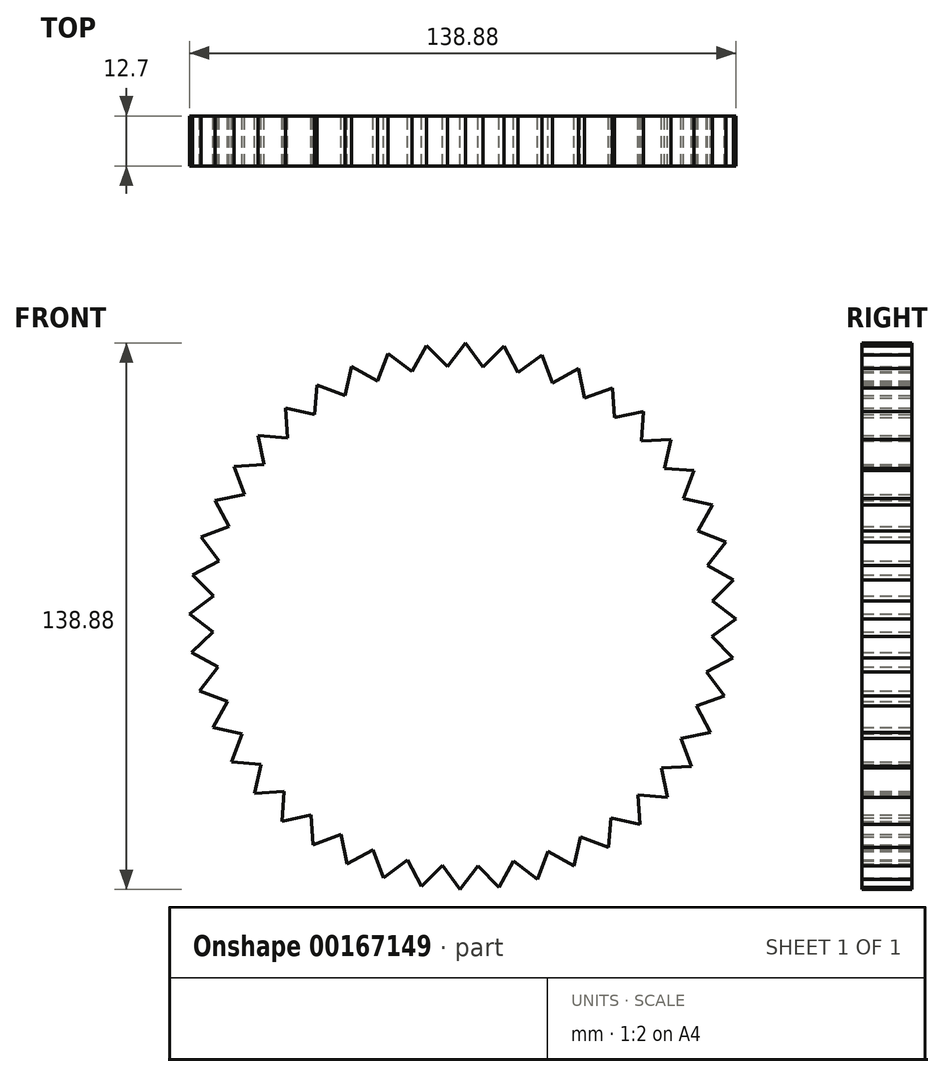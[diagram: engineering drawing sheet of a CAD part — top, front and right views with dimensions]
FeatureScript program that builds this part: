
annotation { "Feature Type Name" : "Feature", "Feature Type Description" : "" }
export const myFeature = defineFeature(function(context is Context, id is Id, definition is map)
    precondition{}
    {
        {
            var Q0;
            Q0=qCreatedBy(makeId("Front.planeOp"),FACE);
            var sketch = newSketch(context, id + "F0", { "sketchPlane" : qUnion([Q0])});
            skCircle(sketch, "E0", {"center": v(0, 0) * mm, "radius": 63.5 * mm});
            skCircle(sketch, "E1", {"center": v(0, 0) * mm, "radius": 25.4 * mm});
            skLineSegment(sketch, "E2", {"start": v(-55.46, 30.93) * mm, "end": v(-58.06, 38.1) * mm});
            skLineSegment(sketch, "E3", {"start": v(-58.06, 38.1) * mm, "end": v(-50.46, 38.55) * mm});
            skLineSegment(sketch, "E4.1.0", {"start": v(-59.3, 22.72) * mm, "end": v(-62.9, 29.44) * mm});
            skLineSegment(sketch, "E4.1.1", {"start": v(-62.9, 29.44) * mm, "end": v(-55.43, 30.98) * mm});
            skLineSegment(sketch, "E4.2.0", {"start": v(-61.93, 14.05) * mm, "end": v(-66.44, 20.2) * mm});
            skLineSegment(sketch, "E4.2.1", {"start": v(-66.44, 20.2) * mm, "end": v(-59.28, 22.77) * mm});
            skLineSegment(sketch, "E4.3.0", {"start": v(-63.3, 5.1) * mm, "end": v(-68.64, 10.53) * mm});
            skLineSegment(sketch, "E4.3.1", {"start": v(-68.64, 10.53) * mm, "end": v(-61.91, 14.1) * mm});
            skLineSegment(sketch, "E4.4.0", {"start": v(-63.38, -3.96) * mm, "end": v(-69.44, 0.65) * mm});
            skLineSegment(sketch, "E4.4.1", {"start": v(-69.44, 0.65) * mm, "end": v(-63.3, 5.15) * mm});
            skLineSegment(sketch, "E4.5.0", {"start": v(-62.17, -12.94) * mm, "end": v(-68.83, -9.24) * mm});
            skLineSegment(sketch, "E4.5.1", {"start": v(-68.83, -9.24) * mm, "end": v(-63.38, -3.9) * mm});
            skLineSegment(sketch, "E4.6.0", {"start": v(-59.7, -21.66) * mm, "end": v(-66.81, -18.94) * mm});
            skLineSegment(sketch, "E4.6.1", {"start": v(-66.81, -18.94) * mm, "end": v(-62.18, -12.89) * mm});
            skLineSegment(sketch, "E4.7.0", {"start": v(-56, -29.93) * mm, "end": v(-63.44, -28.25) * mm});
            skLineSegment(sketch, "E4.7.1", {"start": v(-63.44, -28.25) * mm, "end": v(-59.71, -21.6) * mm});
            skLineSegment(sketch, "E4.8.0", {"start": v(-51.17, -37.6) * mm, "end": v(-58.77, -37) * mm});
            skLineSegment(sketch, "E4.8.1", {"start": v(-58.77, -37) * mm, "end": v(-56.03, -29.88) * mm});
            skLineSegment(sketch, "E4.9.0", {"start": v(-45.3, -44.5) * mm, "end": v(-52.9, -44.98) * mm});
            skLineSegment(sketch, "E4.9.1", {"start": v(-52.9, -44.98) * mm, "end": v(-51.2, -37.55) * mm});
            skLineSegment(sketch, "E4.10.0", {"start": v(-38.5, -50.5) * mm, "end": v(-45.97, -52.05) * mm});
            skLineSegment(sketch, "E4.10.1", {"start": v(-45.97, -52.05) * mm, "end": v(-45.34, -44.46) * mm});
            skLineSegment(sketch, "E4.11.0", {"start": v(-30.93, -55.46) * mm, "end": v(-38.1, -58.06) * mm});
            skLineSegment(sketch, "E4.11.1", {"start": v(-38.1, -58.06) * mm, "end": v(-38.55, -50.46) * mm});
            skLineSegment(sketch, "E4.12.0", {"start": v(-22.72, -59.3) * mm, "end": v(-29.44, -62.9) * mm});
            skLineSegment(sketch, "E4.12.1", {"start": v(-29.44, -62.9) * mm, "end": v(-30.98, -55.43) * mm});
            skLineSegment(sketch, "E4.13.0", {"start": v(-14.05, -61.93) * mm, "end": v(-20.2, -66.44) * mm});
            skLineSegment(sketch, "E4.13.1", {"start": v(-20.2, -66.44) * mm, "end": v(-22.77, -59.28) * mm});
            skLineSegment(sketch, "E4.14.0", {"start": v(-5.1, -63.3) * mm, "end": v(-10.53, -68.64) * mm});
            skLineSegment(sketch, "E4.14.1", {"start": v(-10.53, -68.64) * mm, "end": v(-14.1, -61.91) * mm});
            skLineSegment(sketch, "E4.15.0", {"start": v(3.96, -63.38) * mm, "end": v(-0.65, -69.44) * mm});
            skLineSegment(sketch, "E4.15.1", {"start": v(-0.65, -69.44) * mm, "end": v(-5.15, -63.3) * mm});
            skLineSegment(sketch, "E4.16.0", {"start": v(12.94, -62.17) * mm, "end": v(9.24, -68.83) * mm});
            skLineSegment(sketch, "E4.16.1", {"start": v(9.24, -68.83) * mm, "end": v(3.9, -63.38) * mm});
            skLineSegment(sketch, "E4.17.0", {"start": v(21.66, -59.7) * mm, "end": v(18.94, -66.81) * mm});
            skLineSegment(sketch, "E4.17.1", {"start": v(18.94, -66.81) * mm, "end": v(12.89, -62.18) * mm});
            skLineSegment(sketch, "E4.18.0", {"start": v(29.93, -56) * mm, "end": v(28.25, -63.44) * mm});
            skLineSegment(sketch, "E4.18.1", {"start": v(28.25, -63.44) * mm, "end": v(21.6, -59.71) * mm});
            skLineSegment(sketch, "E4.19.0", {"start": v(37.6, -51.17) * mm, "end": v(37, -58.77) * mm});
            skLineSegment(sketch, "E4.19.1", {"start": v(37, -58.77) * mm, "end": v(29.88, -56.03) * mm});
            skLineSegment(sketch, "E4.20.0", {"start": v(44.5, -45.3) * mm, "end": v(44.98, -52.9) * mm});
            skLineSegment(sketch, "E4.20.1", {"start": v(44.98, -52.9) * mm, "end": v(37.55, -51.2) * mm});
            skLineSegment(sketch, "E4.21.0", {"start": v(50.5, -38.5) * mm, "end": v(52.05, -45.97) * mm});
            skLineSegment(sketch, "E4.21.1", {"start": v(52.05, -45.97) * mm, "end": v(44.46, -45.34) * mm});
            skLineSegment(sketch, "E4.22.0", {"start": v(55.46, -30.93) * mm, "end": v(58.06, -38.1) * mm});
            skLineSegment(sketch, "E4.22.1", {"start": v(58.06, -38.1) * mm, "end": v(50.46, -38.55) * mm});
            skLineSegment(sketch, "E4.23.0", {"start": v(59.3, -22.72) * mm, "end": v(62.9, -29.44) * mm});
            skLineSegment(sketch, "E4.23.1", {"start": v(62.9, -29.44) * mm, "end": v(55.43, -30.98) * mm});
            skLineSegment(sketch, "E4.24.0", {"start": v(61.93, -14.05) * mm, "end": v(66.44, -20.2) * mm});
            skLineSegment(sketch, "E4.24.1", {"start": v(66.44, -20.2) * mm, "end": v(59.28, -22.77) * mm});
            skLineSegment(sketch, "E4.25.0", {"start": v(63.3, -5.1) * mm, "end": v(68.64, -10.53) * mm});
            skLineSegment(sketch, "E4.25.1", {"start": v(68.64, -10.53) * mm, "end": v(61.91, -14.1) * mm});
            skLineSegment(sketch, "E4.26.0", {"start": v(63.38, 3.96) * mm, "end": v(69.44, -0.65) * mm});
            skLineSegment(sketch, "E4.26.1", {"start": v(69.44, -0.65) * mm, "end": v(63.3, -5.15) * mm});
            skLineSegment(sketch, "E4.27.0", {"start": v(62.17, 12.94) * mm, "end": v(68.83, 9.24) * mm});
            skLineSegment(sketch, "E4.27.1", {"start": v(68.83, 9.24) * mm, "end": v(63.38, 3.9) * mm});
            skLineSegment(sketch, "E4.28.0", {"start": v(59.7, 21.66) * mm, "end": v(66.81, 18.94) * mm});
            skLineSegment(sketch, "E4.28.1", {"start": v(66.81, 18.94) * mm, "end": v(62.18, 12.89) * mm});
            skLineSegment(sketch, "E4.29.0", {"start": v(56, 29.93) * mm, "end": v(63.44, 28.25) * mm});
            skLineSegment(sketch, "E4.29.1", {"start": v(63.44, 28.25) * mm, "end": v(59.71, 21.6) * mm});
            skLineSegment(sketch, "E4.30.0", {"start": v(51.17, 37.6) * mm, "end": v(58.77, 37) * mm});
            skLineSegment(sketch, "E4.30.1", {"start": v(58.77, 37) * mm, "end": v(56.03, 29.88) * mm});
            skLineSegment(sketch, "E4.31.0", {"start": v(45.3, 44.5) * mm, "end": v(52.9, 44.98) * mm});
            skLineSegment(sketch, "E4.31.1", {"start": v(52.9, 44.98) * mm, "end": v(51.2, 37.55) * mm});
            skLineSegment(sketch, "E4.32.0", {"start": v(38.5, 50.5) * mm, "end": v(45.97, 52.05) * mm});
            skLineSegment(sketch, "E4.32.1", {"start": v(45.97, 52.05) * mm, "end": v(45.34, 44.46) * mm});
            skLineSegment(sketch, "E4.33.0", {"start": v(30.93, 55.46) * mm, "end": v(38.1, 58.06) * mm});
            skLineSegment(sketch, "E4.33.1", {"start": v(38.1, 58.06) * mm, "end": v(38.55, 50.46) * mm});
            skLineSegment(sketch, "E4.34.0", {"start": v(22.72, 59.3) * mm, "end": v(29.44, 62.9) * mm});
            skLineSegment(sketch, "E4.34.1", {"start": v(29.44, 62.9) * mm, "end": v(30.98, 55.43) * mm});
            skLineSegment(sketch, "E4.35.0", {"start": v(14.05, 61.93) * mm, "end": v(20.2, 66.44) * mm});
            skLineSegment(sketch, "E4.35.1", {"start": v(20.2, 66.44) * mm, "end": v(22.77, 59.28) * mm});
            skLineSegment(sketch, "E4.36.0", {"start": v(5.1, 63.3) * mm, "end": v(10.53, 68.64) * mm});
            skLineSegment(sketch, "E4.36.1", {"start": v(10.53, 68.64) * mm, "end": v(14.1, 61.91) * mm});
            skLineSegment(sketch, "E4.37.0", {"start": v(-3.96, 63.38) * mm, "end": v(0.65, 69.44) * mm});
            skLineSegment(sketch, "E4.37.1", {"start": v(0.65, 69.44) * mm, "end": v(5.15, 63.3) * mm});
            skLineSegment(sketch, "E4.38.0", {"start": v(-12.94, 62.17) * mm, "end": v(-9.24, 68.83) * mm});
            skLineSegment(sketch, "E4.38.1", {"start": v(-9.24, 68.83) * mm, "end": v(-3.9, 63.38) * mm});
            skLineSegment(sketch, "E4.39.0", {"start": v(-21.66, 59.7) * mm, "end": v(-18.94, 66.81) * mm});
            skLineSegment(sketch, "E4.39.1", {"start": v(-18.94, 66.81) * mm, "end": v(-12.89, 62.18) * mm});
            skLineSegment(sketch, "E4.40.0", {"start": v(-29.93, 56) * mm, "end": v(-28.25, 63.44) * mm});
            skLineSegment(sketch, "E4.40.1", {"start": v(-28.25, 63.44) * mm, "end": v(-21.6, 59.71) * mm});
            skLineSegment(sketch, "E4.41.0", {"start": v(-37.6, 51.17) * mm, "end": v(-37, 58.77) * mm});
            skLineSegment(sketch, "E4.41.1", {"start": v(-37, 58.77) * mm, "end": v(-29.88, 56.03) * mm});
            skLineSegment(sketch, "E4.42.0", {"start": v(-44.5, 45.3) * mm, "end": v(-44.98, 52.9) * mm});
            skLineSegment(sketch, "E4.42.1", {"start": v(-44.98, 52.9) * mm, "end": v(-37.55, 51.2) * mm});
            skLineSegment(sketch, "E4.43.0", {"start": v(-50.5, 38.5) * mm, "end": v(-52.05, 45.97) * mm});
            skLineSegment(sketch, "E4.43.1", {"start": v(-52.05, 45.97) * mm, "end": v(-44.46, 45.34) * mm});
            skSolve(sketch);
        }
        {
            var Q0;
            {var subQ5=sQuery(id+"F0.wireOp",EDGE,"E4.16.0");var subQ7=sQuery(id+"F0.wireOp",EDGE,"E0");var subQ8=makeQuery(id+"F0.imprint","INTERSECT",VERTEX,{"derivedFrom":[subQ7,subQ5]});Q0=makeQuery(id+"F0.imprint","IMPRINT",FACE,{"disambiguationData":[TD([[makeQuery(id+"F0.imprint","IMPRINT",EDGE,{"disambiguationData":[TD([[subQ8,-1.0]])],"derivedFrom":subQ7}),-1.0]])]});}
            var Q1;
            Q1=makeQuery(id+"F0.imprint","IMPRINT",FACE,{"disambiguationData":[TD([[makeQuery(id+"F0.imprint","IMPRINT",EDGE,{"derivedFrom":sQuery(id+"F0.wireOp",EDGE,"E1")}),-1.0]])]});
            var Q2;
            {var subQ3=sQuery(id+"F0.wireOp",EDGE,"E4.30.0");var subQ5=sQuery(id+"F0.wireOp",EDGE,"E0");var subQ6=makeQuery(id+"F0.imprint","INTERSECT",VERTEX,{"derivedFrom":[subQ5,subQ3]});Q2=makeQuery(id+"F0.imprint","IMPRINT",FACE,{"disambiguationData":[TD([[makeQuery(id+"F0.imprint","IMPRINT",EDGE,{"disambiguationData":[TD([[subQ6,-1.0]])],"derivedFrom":subQ5}),-1.0]])]});}
            var Q3;
            {var subQ0=sQuery(id+"F0.wireOp",EDGE,"E4.25.0");var subQ1=sQuery(id+"F0.wireOp",EDGE,"E0");var subQ2=makeQuery(id+"F0.imprint","INTERSECT",VERTEX,{"derivedFrom":[subQ1,subQ0]});Q3=makeQuery(id+"F0.imprint","IMPRINT",FACE,{"disambiguationData":[TD([[makeQuery(id+"F0.imprint","IMPRINT",EDGE,{"disambiguationData":[TD([[subQ2,-1.0]])],"derivedFrom":subQ1}),-1.0]])]});}
            var Q4;
            {var subQ3=sQuery(id+"F0.wireOp",EDGE,"E4.27.0");var subQ5=sQuery(id+"F0.wireOp",EDGE,"E0");var subQ6=makeQuery(id+"F0.imprint","INTERSECT",VERTEX,{"derivedFrom":[subQ5,subQ3]});Q4=makeQuery(id+"F0.imprint","IMPRINT",FACE,{"disambiguationData":[TD([[makeQuery(id+"F0.imprint","IMPRINT",EDGE,{"disambiguationData":[TD([[subQ6,-1.0]])],"derivedFrom":subQ5}),-1.0]])]});}
            var Q5;
            {var subQ3=sQuery(id+"F0.wireOp",EDGE,"E4.11.0");var subQ5=sQuery(id+"F0.wireOp",EDGE,"E0");var subQ6=makeQuery(id+"F0.imprint","INTERSECT",VERTEX,{"derivedFrom":[subQ5,subQ3]});Q5=makeQuery(id+"F0.imprint","IMPRINT",FACE,{"disambiguationData":[TD([[makeQuery(id+"F0.imprint","IMPRINT",EDGE,{"disambiguationData":[TD([[subQ6,-1.0]])],"derivedFrom":subQ5}),-1.0]])]});}
            var Q6;
            {var subQ3=sQuery(id+"F0.wireOp",EDGE,"E4.17.0");var subQ5=sQuery(id+"F0.wireOp",EDGE,"E0");var subQ6=makeQuery(id+"F0.imprint","INTERSECT",VERTEX,{"derivedFrom":[subQ5,subQ3]});Q6=makeQuery(id+"F0.imprint","IMPRINT",FACE,{"disambiguationData":[TD([[makeQuery(id+"F0.imprint","IMPRINT",EDGE,{"disambiguationData":[TD([[subQ6,-1.0]])],"derivedFrom":subQ5}),-1.0]])]});}
            var Q7;
            {var subQ3=sQuery(id+"F0.wireOp",EDGE,"E4.21.0");var subQ7=sQuery(id+"F0.wireOp",EDGE,"E0");var subQ8=makeQuery(id+"F0.imprint","INTERSECT",VERTEX,{"derivedFrom":[subQ7,subQ3]});Q7=makeQuery(id+"F0.imprint","IMPRINT",FACE,{"disambiguationData":[TD([[makeQuery(id+"F0.imprint","IMPRINT",EDGE,{"disambiguationData":[TD([[subQ8,-1.0]])],"derivedFrom":subQ7}),-1.0]])]});}
            var Q8;
            Q8=makeQuery(id+"F0.imprint","IMPRINT",FACE,{"disambiguationData":[TD([[makeQuery(id+"F0.imprint","IMPRINT",EDGE,{"derivedFrom":sQuery(id+"F0.wireOp",EDGE,"E1")}),1.0]])]});
            var Q9;
            {var subQ3=sQuery(id+"F0.wireOp",EDGE,"E4.23.0");var subQ5=sQuery(id+"F0.wireOp",EDGE,"E0");var subQ6=makeQuery(id+"F0.imprint","INTERSECT",VERTEX,{"derivedFrom":[subQ5,subQ3]});Q9=makeQuery(id+"F0.imprint","IMPRINT",FACE,{"disambiguationData":[TD([[makeQuery(id+"F0.imprint","IMPRINT",EDGE,{"disambiguationData":[TD([[subQ6,-1.0]])],"derivedFrom":subQ5}),-1.0]])]});}
            var Q10;
            {var subQ3=sQuery(id+"F0.wireOp",EDGE,"E4.24.0");var subQ7=sQuery(id+"F0.wireOp",EDGE,"E0");var subQ8=makeQuery(id+"F0.imprint","INTERSECT",VERTEX,{"derivedFrom":[subQ7,subQ3]});Q10=makeQuery(id+"F0.imprint","IMPRINT",FACE,{"disambiguationData":[TD([[makeQuery(id+"F0.imprint","IMPRINT",EDGE,{"disambiguationData":[TD([[subQ8,-1.0]])],"derivedFrom":subQ7}),-1.0]])]});}
            var Q11;
            {var subQ3=sQuery(id+"F0.wireOp",EDGE,"E4.10.0");var subQ7=sQuery(id+"F0.wireOp",EDGE,"E0");var subQ8=makeQuery(id+"F0.imprint","INTERSECT",VERTEX,{"derivedFrom":[subQ7,subQ3]});Q11=makeQuery(id+"F0.imprint","IMPRINT",FACE,{"disambiguationData":[TD([[makeQuery(id+"F0.imprint","IMPRINT",EDGE,{"disambiguationData":[TD([[subQ8,-1.0]])],"derivedFrom":subQ7}),-1.0]])]});}
            var Q12;
            {var subQ3=sQuery(id+"F0.wireOp",EDGE,"E4.12.0");var subQ5=sQuery(id+"F0.wireOp",EDGE,"E0");var subQ6=makeQuery(id+"F0.imprint","INTERSECT",VERTEX,{"derivedFrom":[subQ5,subQ3]});Q12=makeQuery(id+"F0.imprint","IMPRINT",FACE,{"disambiguationData":[TD([[makeQuery(id+"F0.imprint","IMPRINT",EDGE,{"disambiguationData":[TD([[subQ6,-1.0]])],"derivedFrom":subQ5}),-1.0]])]});}
            var Q13;
            {var subQ3=sQuery(id+"F0.wireOp",EDGE,"E4.20.0");var subQ7=sQuery(id+"F0.wireOp",EDGE,"E0");var subQ9=makeQuery(id+"F0.imprint","INTERSECT",VERTEX,{"derivedFrom":[subQ7,subQ3]});Q13=makeQuery(id+"F0.imprint","IMPRINT",FACE,{"disambiguationData":[TD([[makeQuery(id+"F0.imprint","IMPRINT",EDGE,{"disambiguationData":[TD([[subQ9,-1.0]])],"derivedFrom":subQ7}),-1.0]])]});}
            var Q14;
            {var subQ3=sQuery(id+"F0.wireOp",EDGE,"E4.29.0");var subQ5=sQuery(id+"F0.wireOp",EDGE,"E0");var subQ6=makeQuery(id+"F0.imprint","INTERSECT",VERTEX,{"derivedFrom":[subQ5,subQ3]});Q14=makeQuery(id+"F0.imprint","IMPRINT",FACE,{"disambiguationData":[TD([[makeQuery(id+"F0.imprint","IMPRINT",EDGE,{"disambiguationData":[TD([[subQ6,-1.0]])],"derivedFrom":subQ5}),-1.0]])]});}
            var Q15;
            {var subQ3=sQuery(id+"F0.wireOp",EDGE,"E4.26.0");var subQ7=sQuery(id+"F0.wireOp",EDGE,"E0");var subQ8=makeQuery(id+"F0.imprint","INTERSECT",VERTEX,{"derivedFrom":[subQ7,subQ3]});Q15=makeQuery(id+"F0.imprint","IMPRINT",FACE,{"disambiguationData":[TD([[makeQuery(id+"F0.imprint","IMPRINT",EDGE,{"disambiguationData":[TD([[subQ8,-1.0]])],"derivedFrom":subQ7}),-1.0]])]});}
            var Q16;
            {var subQ3=sQuery(id+"F0.wireOp",EDGE,"E4.19.0");var subQ7=sQuery(id+"F0.wireOp",EDGE,"E0");var subQ8=makeQuery(id+"F0.imprint","INTERSECT",VERTEX,{"derivedFrom":[subQ7,subQ3]});Q16=makeQuery(id+"F0.imprint","IMPRINT",FACE,{"disambiguationData":[TD([[makeQuery(id+"F0.imprint","IMPRINT",EDGE,{"disambiguationData":[TD([[subQ8,-1.0]])],"derivedFrom":subQ7}),-1.0]])]});}
            var Q17;
            {var subQ0=sQuery(id+"F0.wireOp",EDGE,"E4.18.0");var subQ1=sQuery(id+"F0.wireOp",EDGE,"E0");var subQ2=makeQuery(id+"F0.imprint","INTERSECT",VERTEX,{"derivedFrom":[subQ1,subQ0]});Q17=makeQuery(id+"F0.imprint","IMPRINT",FACE,{"disambiguationData":[TD([[makeQuery(id+"F0.imprint","IMPRINT",EDGE,{"disambiguationData":[TD([[subQ2,-1.0]])],"derivedFrom":subQ1}),-1.0]])]});}
            var Q18;
            {var subQ3=sQuery(id+"F0.wireOp",EDGE,"E4.22.0");var subQ7=sQuery(id+"F0.wireOp",EDGE,"E0");var subQ8=makeQuery(id+"F0.imprint","INTERSECT",VERTEX,{"derivedFrom":[subQ7,subQ3]});Q18=makeQuery(id+"F0.imprint","IMPRINT",FACE,{"disambiguationData":[TD([[makeQuery(id+"F0.imprint","IMPRINT",EDGE,{"disambiguationData":[TD([[subQ8,-1.0]])],"derivedFrom":subQ7}),-1.0]])]});}
            var Q19;
            {var subQ3=sQuery(id+"F0.wireOp",EDGE,"E4.28.0");var subQ7=sQuery(id+"F0.wireOp",EDGE,"E0");var subQ8=makeQuery(id+"F0.imprint","INTERSECT",VERTEX,{"derivedFrom":[subQ7,subQ3]});Q19=makeQuery(id+"F0.imprint","IMPRINT",FACE,{"disambiguationData":[TD([[makeQuery(id+"F0.imprint","IMPRINT",EDGE,{"disambiguationData":[TD([[subQ8,-1.0]])],"derivedFrom":subQ7}),-1.0]])]});}
            var Q20;
            {var subQ3=sQuery(id+"F0.wireOp",EDGE,"E4.15.0");var subQ7=sQuery(id+"F0.wireOp",EDGE,"E0");var subQ8=makeQuery(id+"F0.imprint","INTERSECT",VERTEX,{"derivedFrom":[subQ7,subQ3]});Q20=makeQuery(id+"F0.imprint","IMPRINT",FACE,{"disambiguationData":[TD([[makeQuery(id+"F0.imprint","IMPRINT",EDGE,{"disambiguationData":[TD([[subQ8,-1.0]])],"derivedFrom":subQ7}),-1.0]])]});}
            var Q21;
            {var subQ3=sQuery(id+"F0.wireOp",EDGE,"E4.13.0");var subQ7=sQuery(id+"F0.wireOp",EDGE,"E0");var subQ8=makeQuery(id+"F0.imprint","INTERSECT",VERTEX,{"derivedFrom":[subQ7,subQ3]});Q21=makeQuery(id+"F0.imprint","IMPRINT",FACE,{"disambiguationData":[TD([[makeQuery(id+"F0.imprint","IMPRINT",EDGE,{"disambiguationData":[TD([[subQ8,-1.0]])],"derivedFrom":subQ7}),-1.0]])]});}
            var Q22;
            {var subQ0=sQuery(id+"F0.wireOp",EDGE,"E4.25.0");var subQ1=sQuery(id+"F0.wireOp",EDGE,"E0");var subQ2=makeQuery(id+"F0.imprint","INTERSECT",VERTEX,{"derivedFrom":[subQ1,subQ0]});Q22=makeQuery(id+"F0.imprint","IMPRINT",FACE,{"disambiguationData":[TD([[makeQuery(id+"F0.imprint","IMPRINT",EDGE,{"disambiguationData":[TD([[subQ2,1.0]])],"derivedFrom":subQ1}),-1.0]])]});}
            var Q23;
            {var subQ0=sQuery(id+"F0.wireOp",EDGE,"E4.24.0");var subQ1=sQuery(id+"F0.wireOp",EDGE,"E0");var subQ2=makeQuery(id+"F0.imprint","INTERSECT",VERTEX,{"derivedFrom":[subQ1,subQ0]});Q23=makeQuery(id+"F0.imprint","IMPRINT",FACE,{"disambiguationData":[TD([[makeQuery(id+"F0.imprint","IMPRINT",EDGE,{"disambiguationData":[TD([[subQ2,1.0]])],"derivedFrom":subQ1}),-1.0]])]});}
            var Q24;
            {var subQ0=sQuery(id+"F0.wireOp",EDGE,"E4.18.0");var subQ1=sQuery(id+"F0.wireOp",EDGE,"E0");var subQ2=makeQuery(id+"F0.imprint","INTERSECT",VERTEX,{"derivedFrom":[subQ1,subQ0]});Q24=makeQuery(id+"F0.imprint","IMPRINT",FACE,{"disambiguationData":[TD([[makeQuery(id+"F0.imprint","IMPRINT",EDGE,{"disambiguationData":[TD([[subQ2,1.0]])],"derivedFrom":subQ1}),-1.0]])]});}
            var Q25;
            {var subQ0=sQuery(id+"F0.wireOp",EDGE,"E4.12.0");var subQ1=sQuery(id+"F0.wireOp",EDGE,"E0");var subQ2=makeQuery(id+"F0.imprint","INTERSECT",VERTEX,{"derivedFrom":[subQ1,subQ0]});Q25=makeQuery(id+"F0.imprint","IMPRINT",FACE,{"disambiguationData":[TD([[makeQuery(id+"F0.imprint","IMPRINT",EDGE,{"disambiguationData":[TD([[subQ2,1.0]])],"derivedFrom":subQ1}),-1.0]])]});}
            var Q26;
            {var subQ0=sQuery(id+"F0.wireOp",EDGE,"E4.30.0");var subQ1=sQuery(id+"F0.wireOp",EDGE,"E0");var subQ2=makeQuery(id+"F0.imprint","INTERSECT",VERTEX,{"derivedFrom":[subQ1,subQ0]});Q26=makeQuery(id+"F0.imprint","IMPRINT",FACE,{"disambiguationData":[TD([[makeQuery(id+"F0.imprint","IMPRINT",EDGE,{"disambiguationData":[TD([[subQ2,1.0]])],"derivedFrom":subQ1}),-1.0]])]});}
            var Q27;
            {var subQ0=sQuery(id+"F0.wireOp",EDGE,"E4.26.0");var subQ1=sQuery(id+"F0.wireOp",EDGE,"E0");var subQ2=makeQuery(id+"F0.imprint","INTERSECT",VERTEX,{"derivedFrom":[subQ1,subQ0]});Q27=makeQuery(id+"F0.imprint","IMPRINT",FACE,{"disambiguationData":[TD([[makeQuery(id+"F0.imprint","IMPRINT",EDGE,{"disambiguationData":[TD([[subQ2,1.0]])],"derivedFrom":subQ1}),-1.0]])]});}
            var Q28;
            {var subQ0=sQuery(id+"F0.wireOp",EDGE,"E4.23.0");var subQ1=sQuery(id+"F0.wireOp",EDGE,"E0");var subQ2=makeQuery(id+"F0.imprint","INTERSECT",VERTEX,{"derivedFrom":[subQ1,subQ0]});Q28=makeQuery(id+"F0.imprint","IMPRINT",FACE,{"disambiguationData":[TD([[makeQuery(id+"F0.imprint","IMPRINT",EDGE,{"disambiguationData":[TD([[subQ2,1.0]])],"derivedFrom":subQ1}),-1.0]])]});}
            var Q29;
            {var subQ0=sQuery(id+"F0.wireOp",EDGE,"E4.29.0");var subQ1=sQuery(id+"F0.wireOp",EDGE,"E0");var subQ2=makeQuery(id+"F0.imprint","INTERSECT",VERTEX,{"derivedFrom":[subQ1,subQ0]});Q29=makeQuery(id+"F0.imprint","IMPRINT",FACE,{"disambiguationData":[TD([[makeQuery(id+"F0.imprint","IMPRINT",EDGE,{"disambiguationData":[TD([[subQ2,1.0]])],"derivedFrom":subQ1}),-1.0]])]});}
            var Q30;
            {var subQ0=sQuery(id+"F0.wireOp",EDGE,"E4.17.0");var subQ1=sQuery(id+"F0.wireOp",EDGE,"E0");var subQ2=makeQuery(id+"F0.imprint","INTERSECT",VERTEX,{"derivedFrom":[subQ1,subQ0]});Q30=makeQuery(id+"F0.imprint","IMPRINT",FACE,{"disambiguationData":[TD([[makeQuery(id+"F0.imprint","IMPRINT",EDGE,{"disambiguationData":[TD([[subQ2,1.0]])],"derivedFrom":subQ1}),-1.0]])]});}
            var Q31;
            {var subQ0=sQuery(id+"F0.wireOp",EDGE,"E4.21.0");var subQ1=sQuery(id+"F0.wireOp",EDGE,"E0");var subQ2=makeQuery(id+"F0.imprint","INTERSECT",VERTEX,{"derivedFrom":[subQ1,subQ0]});Q31=makeQuery(id+"F0.imprint","IMPRINT",FACE,{"disambiguationData":[TD([[makeQuery(id+"F0.imprint","IMPRINT",EDGE,{"disambiguationData":[TD([[subQ2,1.0]])],"derivedFrom":subQ1}),-1.0]])]});}
            var Q32;
            {var subQ0=sQuery(id+"F0.wireOp",EDGE,"E4.28.0");var subQ1=sQuery(id+"F0.wireOp",EDGE,"E0");var subQ2=makeQuery(id+"F0.imprint","INTERSECT",VERTEX,{"derivedFrom":[subQ1,subQ0]});Q32=makeQuery(id+"F0.imprint","IMPRINT",FACE,{"disambiguationData":[TD([[makeQuery(id+"F0.imprint","IMPRINT",EDGE,{"disambiguationData":[TD([[subQ2,1.0]])],"derivedFrom":subQ1}),-1.0]])]});}
            var Q33;
            {var subQ0=sQuery(id+"F0.wireOp",EDGE,"E4.22.0");var subQ1=sQuery(id+"F0.wireOp",EDGE,"E0");var subQ2=makeQuery(id+"F0.imprint","INTERSECT",VERTEX,{"derivedFrom":[subQ1,subQ0]});Q33=makeQuery(id+"F0.imprint","IMPRINT",FACE,{"disambiguationData":[TD([[makeQuery(id+"F0.imprint","IMPRINT",EDGE,{"disambiguationData":[TD([[subQ2,1.0]])],"derivedFrom":subQ1}),-1.0]])]});}
            var Q34;
            {var subQ0=sQuery(id+"F0.wireOp",EDGE,"E4.20.0");var subQ1=sQuery(id+"F0.wireOp",EDGE,"E0");var subQ2=makeQuery(id+"F0.imprint","INTERSECT",VERTEX,{"derivedFrom":[subQ1,subQ0]});Q34=makeQuery(id+"F0.imprint","IMPRINT",FACE,{"disambiguationData":[TD([[makeQuery(id+"F0.imprint","IMPRINT",EDGE,{"disambiguationData":[TD([[subQ2,1.0]])],"derivedFrom":subQ1}),-1.0]])]});}
            var Q35;
            {var subQ0=sQuery(id+"F0.wireOp",EDGE,"E4.19.0");var subQ1=sQuery(id+"F0.wireOp",EDGE,"E0");var subQ2=makeQuery(id+"F0.imprint","INTERSECT",VERTEX,{"derivedFrom":[subQ1,subQ0]});Q35=makeQuery(id+"F0.imprint","IMPRINT",FACE,{"disambiguationData":[TD([[makeQuery(id+"F0.imprint","IMPRINT",EDGE,{"disambiguationData":[TD([[subQ2,1.0]])],"derivedFrom":subQ1}),-1.0]])]});}
            var Q36;
            {var subQ0=sQuery(id+"F0.wireOp",EDGE,"E4.11.0");var subQ1=sQuery(id+"F0.wireOp",EDGE,"E0");var subQ2=makeQuery(id+"F0.imprint","INTERSECT",VERTEX,{"derivedFrom":[subQ1,subQ0]});Q36=makeQuery(id+"F0.imprint","IMPRINT",FACE,{"disambiguationData":[TD([[makeQuery(id+"F0.imprint","IMPRINT",EDGE,{"disambiguationData":[TD([[subQ2,1.0]])],"derivedFrom":subQ1}),-1.0]])]});}
            var Q37;
            {var subQ0=sQuery(id+"F0.wireOp",EDGE,"E4.27.0");var subQ1=sQuery(id+"F0.wireOp",EDGE,"E0");var subQ2=makeQuery(id+"F0.imprint","INTERSECT",VERTEX,{"derivedFrom":[subQ1,subQ0]});Q37=makeQuery(id+"F0.imprint","IMPRINT",FACE,{"disambiguationData":[TD([[makeQuery(id+"F0.imprint","IMPRINT",EDGE,{"disambiguationData":[TD([[subQ2,1.0]])],"derivedFrom":subQ1}),-1.0]])]});}
            var Q38;
            {var subQ0=sQuery(id+"F0.wireOp",EDGE,"E4.13.0");var subQ1=sQuery(id+"F0.wireOp",EDGE,"E0");var subQ2=makeQuery(id+"F0.imprint","INTERSECT",VERTEX,{"derivedFrom":[subQ1,subQ0]});Q38=makeQuery(id+"F0.imprint","IMPRINT",FACE,{"disambiguationData":[TD([[makeQuery(id+"F0.imprint","IMPRINT",EDGE,{"disambiguationData":[TD([[subQ2,1.0]])],"derivedFrom":subQ1}),-1.0]])]});}
            var Q39;
            {var subQ0=sQuery(id+"F0.wireOp",EDGE,"E4.16.0");var subQ1=sQuery(id+"F0.wireOp",EDGE,"E0");var subQ2=makeQuery(id+"F0.imprint","INTERSECT",VERTEX,{"derivedFrom":[subQ1,subQ0]});Q39=makeQuery(id+"F0.imprint","IMPRINT",FACE,{"disambiguationData":[TD([[makeQuery(id+"F0.imprint","IMPRINT",EDGE,{"disambiguationData":[TD([[subQ2,1.0]])],"derivedFrom":subQ1}),-1.0]])]});}
            var Q40;
            {var subQ5=sQuery(id+"F0.wireOp",EDGE,"E4.32.0");var subQ7=sQuery(id+"F0.wireOp",EDGE,"E0");var subQ8=makeQuery(id+"F0.imprint","INTERSECT",VERTEX,{"derivedFrom":[subQ7,subQ5]});Q40=makeQuery(id+"F0.imprint","IMPRINT",FACE,{"disambiguationData":[TD([[makeQuery(id+"F0.imprint","IMPRINT",EDGE,{"disambiguationData":[TD([[subQ8,-1.0]])],"derivedFrom":subQ7}),-1.0]])]});}
            var Q41;
            {var subQ3=sQuery(id+"F0.wireOp",EDGE,"E4.4.0");var subQ7=sQuery(id+"F0.wireOp",EDGE,"E0");var subQ8=makeQuery(id+"F0.imprint","INTERSECT",VERTEX,{"derivedFrom":[subQ7,subQ3]});Q41=makeQuery(id+"F0.imprint","IMPRINT",FACE,{"disambiguationData":[TD([[makeQuery(id+"F0.imprint","IMPRINT",EDGE,{"disambiguationData":[TD([[subQ8,-1.0]])],"derivedFrom":subQ7}),-1.0]])]});}
            var Q42;
            {var subQ5=sQuery(id+"F0.wireOp",EDGE,"E4.1.1");var subQ6=sQuery(id+"F0.wireOp",EDGE,"E0");var subQ7=makeQuery(id+"F0.imprint","INTERSECT",VERTEX,{"derivedFrom":[subQ6,subQ5]});Q42=makeQuery(id+"F0.imprint","IMPRINT",FACE,{"disambiguationData":[TD([[makeQuery(id+"F0.imprint","IMPRINT",EDGE,{"disambiguationData":[TD([[subQ7,1.0]])],"derivedFrom":subQ6}),-1.0]])]});}
            var Q43;
            {var subQ3=sQuery(id+"F0.wireOp",EDGE,"E4.39.0");var subQ7=sQuery(id+"F0.wireOp",EDGE,"E0");var subQ8=makeQuery(id+"F0.imprint","INTERSECT",VERTEX,{"derivedFrom":[subQ7,subQ3]});Q43=makeQuery(id+"F0.imprint","IMPRINT",FACE,{"disambiguationData":[TD([[makeQuery(id+"F0.imprint","IMPRINT",EDGE,{"disambiguationData":[TD([[subQ8,-1.0]])],"derivedFrom":subQ7}),-1.0]])]});}
            var Q44;
            {var subQ3=sQuery(id+"F0.wireOp",EDGE,"E4.7.0");var subQ7=sQuery(id+"F0.wireOp",EDGE,"E0");var subQ8=makeQuery(id+"F0.imprint","INTERSECT",VERTEX,{"derivedFrom":[subQ7,subQ3]});Q44=makeQuery(id+"F0.imprint","IMPRINT",FACE,{"disambiguationData":[TD([[makeQuery(id+"F0.imprint","IMPRINT",EDGE,{"disambiguationData":[TD([[subQ8,-1.0]])],"derivedFrom":subQ7}),-1.0]])]});}
            var Q45;
            {var subQ0=sQuery(id+"F0.wireOp",EDGE,"E4.33.0");var subQ1=sQuery(id+"F0.wireOp",EDGE,"E0");var subQ2=makeQuery(id+"F0.imprint","INTERSECT",VERTEX,{"derivedFrom":[subQ1,subQ0]});Q45=makeQuery(id+"F0.imprint","IMPRINT",FACE,{"disambiguationData":[TD([[makeQuery(id+"F0.imprint","IMPRINT",EDGE,{"disambiguationData":[TD([[subQ2,-1.0]])],"derivedFrom":subQ1}),-1.0]])]});}
            var Q46;
            {var subQ3=sQuery(id+"F0.wireOp",EDGE,"E4.35.0");var subQ7=sQuery(id+"F0.wireOp",EDGE,"E0");var subQ9=makeQuery(id+"F0.imprint","INTERSECT",VERTEX,{"derivedFrom":[subQ7,subQ3]});Q46=makeQuery(id+"F0.imprint","IMPRINT",FACE,{"disambiguationData":[TD([[makeQuery(id+"F0.imprint","IMPRINT",EDGE,{"disambiguationData":[TD([[subQ9,-1.0]])],"derivedFrom":subQ7}),-1.0]])]});}
            var Q47;
            {var subQ0=sQuery(id+"F0.wireOp",EDGE,"E4.6.0");var subQ1=sQuery(id+"F0.wireOp",EDGE,"E0");var subQ2=makeQuery(id+"F0.imprint","INTERSECT",VERTEX,{"derivedFrom":[subQ1,subQ0]});Q47=makeQuery(id+"F0.imprint","IMPRINT",FACE,{"disambiguationData":[TD([[makeQuery(id+"F0.imprint","IMPRINT",EDGE,{"disambiguationData":[TD([[subQ2,-1.0]])],"derivedFrom":subQ1}),-1.0]])]});}
            var Q48;
            {var subQ3=sQuery(id+"F0.wireOp",EDGE,"E4.3.0");var subQ7=sQuery(id+"F0.wireOp",EDGE,"E0");var subQ9=makeQuery(id+"F0.imprint","INTERSECT",VERTEX,{"derivedFrom":[subQ7,subQ3]});Q48=makeQuery(id+"F0.imprint","IMPRINT",FACE,{"disambiguationData":[TD([[makeQuery(id+"F0.imprint","IMPRINT",EDGE,{"disambiguationData":[TD([[subQ9,-1.0]])],"derivedFrom":subQ7}),-1.0]])]});}
            var Q49;
            {var subQ3=sQuery(id+"F0.wireOp",EDGE,"E4.40.0");var subQ7=sQuery(id+"F0.wireOp",EDGE,"E0");var subQ8=makeQuery(id+"F0.imprint","INTERSECT",VERTEX,{"derivedFrom":[subQ7,subQ3]});Q49=makeQuery(id+"F0.imprint","IMPRINT",FACE,{"disambiguationData":[TD([[makeQuery(id+"F0.imprint","IMPRINT",EDGE,{"disambiguationData":[TD([[subQ8,-1.0]])],"derivedFrom":subQ7}),-1.0]])]});}
            var Q50;
            {var subQ0=sQuery(id+"F0.wireOp",EDGE,"E4.1.0");var subQ1=sQuery(id+"F0.wireOp",EDGE,"E0");var subQ2=makeQuery(id+"F0.imprint","INTERSECT",VERTEX,{"derivedFrom":[subQ1,subQ0]});Q50=makeQuery(id+"F0.imprint","IMPRINT",FACE,{"disambiguationData":[TD([[makeQuery(id+"F0.imprint","IMPRINT",EDGE,{"disambiguationData":[TD([[subQ2,-1.0]])],"derivedFrom":subQ1}),-1.0]])]});}
            var Q51;
            {var subQ3=sQuery(id+"F0.wireOp",EDGE,"E4.37.0");var subQ7=sQuery(id+"F0.wireOp",EDGE,"E0");var subQ9=makeQuery(id+"F0.imprint","INTERSECT",VERTEX,{"derivedFrom":[subQ7,subQ3]});Q51=makeQuery(id+"F0.imprint","IMPRINT",FACE,{"disambiguationData":[TD([[makeQuery(id+"F0.imprint","IMPRINT",EDGE,{"disambiguationData":[TD([[subQ9,-1.0]])],"derivedFrom":subQ7}),-1.0]])]});}
            var Q52;
            {var subQ0=sQuery(id+"F0.wireOp",EDGE,"E4.9.0");var subQ1=sQuery(id+"F0.wireOp",EDGE,"E0");var subQ2=makeQuery(id+"F0.imprint","INTERSECT",VERTEX,{"derivedFrom":[subQ1,subQ0]});Q52=makeQuery(id+"F0.imprint","IMPRINT",FACE,{"disambiguationData":[TD([[makeQuery(id+"F0.imprint","IMPRINT",EDGE,{"disambiguationData":[TD([[subQ2,-1.0]])],"derivedFrom":subQ1}),-1.0]])]});}
            var Q53;
            {var subQ3=sQuery(id+"F0.wireOp",EDGE,"E4.41.0");var subQ7=sQuery(id+"F0.wireOp",EDGE,"E0");var subQ8=makeQuery(id+"F0.imprint","INTERSECT",VERTEX,{"derivedFrom":[subQ7,subQ3]});Q53=makeQuery(id+"F0.imprint","IMPRINT",FACE,{"disambiguationData":[TD([[makeQuery(id+"F0.imprint","IMPRINT",EDGE,{"disambiguationData":[TD([[subQ8,-1.0]])],"derivedFrom":subQ7}),-1.0]])]});}
            var Q54;
            {var subQ0=sQuery(id+"F0.wireOp",EDGE,"E4.34.0");var subQ1=sQuery(id+"F0.wireOp",EDGE,"E0");var subQ2=makeQuery(id+"F0.imprint","INTERSECT",VERTEX,{"derivedFrom":[subQ1,subQ0]});Q54=makeQuery(id+"F0.imprint","IMPRINT",FACE,{"disambiguationData":[TD([[makeQuery(id+"F0.imprint","IMPRINT",EDGE,{"disambiguationData":[TD([[subQ2,-1.0]])],"derivedFrom":subQ1}),-1.0]])]});}
            var Q55;
            {var subQ3=sQuery(id+"F0.wireOp",EDGE,"E4.38.0");var subQ7=sQuery(id+"F0.wireOp",EDGE,"E0");var subQ8=makeQuery(id+"F0.imprint","INTERSECT",VERTEX,{"derivedFrom":[subQ7,subQ3]});Q55=makeQuery(id+"F0.imprint","IMPRINT",FACE,{"disambiguationData":[TD([[makeQuery(id+"F0.imprint","IMPRINT",EDGE,{"disambiguationData":[TD([[subQ8,-1.0]])],"derivedFrom":subQ7}),-1.0]])]});}
            var Q56;
            {var subQ1=sQuery(id+"F0.wireOp",EDGE,"E0");var subQ5=sQuery(id+"F0.wireOp",EDGE,"E3");var subQ6=makeQuery(id+"F0.imprint","INTERSECT",VERTEX,{"derivedFrom":[subQ1,subQ5]});Q56=makeQuery(id+"F0.imprint","IMPRINT",FACE,{"disambiguationData":[TD([[makeQuery(id+"F0.imprint","IMPRINT",EDGE,{"disambiguationData":[TD([[subQ6,1.0]])],"derivedFrom":subQ1}),-1.0]])]});}
            var Q57;
            {var subQ3=sQuery(id+"F0.wireOp",EDGE,"E4.2.0");var subQ7=sQuery(id+"F0.wireOp",EDGE,"E0");var subQ8=makeQuery(id+"F0.imprint","INTERSECT",VERTEX,{"derivedFrom":[subQ7,subQ3]});Q57=makeQuery(id+"F0.imprint","IMPRINT",FACE,{"disambiguationData":[TD([[makeQuery(id+"F0.imprint","IMPRINT",EDGE,{"disambiguationData":[TD([[subQ8,-1.0]])],"derivedFrom":subQ7}),-1.0]])]});}
            var Q58;
            {var subQ3=sQuery(id+"F0.wireOp",EDGE,"E4.36.0");var subQ7=sQuery(id+"F0.wireOp",EDGE,"E0");var subQ8=makeQuery(id+"F0.imprint","INTERSECT",VERTEX,{"derivedFrom":[subQ7,subQ3]});Q58=makeQuery(id+"F0.imprint","IMPRINT",FACE,{"disambiguationData":[TD([[makeQuery(id+"F0.imprint","IMPRINT",EDGE,{"disambiguationData":[TD([[subQ8,-1.0]])],"derivedFrom":subQ7}),-1.0]])]});}
            var Q59;
            {var subQ3=sQuery(id+"F0.wireOp",EDGE,"E4.31.0");var subQ7=sQuery(id+"F0.wireOp",EDGE,"E0");var subQ8=makeQuery(id+"F0.imprint","INTERSECT",VERTEX,{"derivedFrom":[subQ7,subQ3]});Q59=makeQuery(id+"F0.imprint","IMPRINT",FACE,{"disambiguationData":[TD([[makeQuery(id+"F0.imprint","IMPRINT",EDGE,{"disambiguationData":[TD([[subQ8,-1.0]])],"derivedFrom":subQ7}),-1.0]])]});}
            var Q60;
            {var subQ3=sQuery(id+"F0.wireOp",EDGE,"E2");var subQ7=sQuery(id+"F0.wireOp",EDGE,"E0");var subQ8=makeQuery(id+"F0.imprint","INTERSECT",VERTEX,{"derivedFrom":[subQ7,subQ3]});Q60=makeQuery(id+"F0.imprint","IMPRINT",FACE,{"disambiguationData":[TD([[makeQuery(id+"F0.imprint","IMPRINT",EDGE,{"disambiguationData":[TD([[subQ8,-1.0]])],"derivedFrom":subQ7}),-1.0]])]});}
            var Q61;
            {var subQ3=sQuery(id+"F0.wireOp",EDGE,"E4.14.0");var subQ5=sQuery(id+"F0.wireOp",EDGE,"E0");var subQ6=makeQuery(id+"F0.imprint","INTERSECT",VERTEX,{"derivedFrom":[subQ5,subQ3]});Q61=makeQuery(id+"F0.imprint","IMPRINT",FACE,{"disambiguationData":[TD([[makeQuery(id+"F0.imprint","IMPRINT",EDGE,{"disambiguationData":[TD([[subQ6,-1.0]])],"derivedFrom":subQ5}),-1.0]])]});}
            var Q62;
            {var subQ3=sQuery(id+"F0.wireOp",EDGE,"E4.5.0");var subQ7=sQuery(id+"F0.wireOp",EDGE,"E0");var subQ9=makeQuery(id+"F0.imprint","INTERSECT",VERTEX,{"derivedFrom":[subQ7,subQ3]});Q62=makeQuery(id+"F0.imprint","IMPRINT",FACE,{"disambiguationData":[TD([[makeQuery(id+"F0.imprint","IMPRINT",EDGE,{"disambiguationData":[TD([[subQ9,-1.0]])],"derivedFrom":subQ7}),-1.0]])]});}
            var Q63;
            {var subQ3=sQuery(id+"F0.wireOp",EDGE,"E4.8.0");var subQ7=sQuery(id+"F0.wireOp",EDGE,"E0");var subQ8=makeQuery(id+"F0.imprint","INTERSECT",VERTEX,{"derivedFrom":[subQ7,subQ3]});Q63=makeQuery(id+"F0.imprint","IMPRINT",FACE,{"disambiguationData":[TD([[makeQuery(id+"F0.imprint","IMPRINT",EDGE,{"disambiguationData":[TD([[subQ8,-1.0]])],"derivedFrom":subQ7}),-1.0]])]});}
            var Q64;
            {var subQ0=sQuery(id+"F0.wireOp",EDGE,"E4.38.0");var subQ1=sQuery(id+"F0.wireOp",EDGE,"E0");var subQ2=makeQuery(id+"F0.imprint","INTERSECT",VERTEX,{"derivedFrom":[subQ1,subQ0]});Q64=makeQuery(id+"F0.imprint","IMPRINT",FACE,{"disambiguationData":[TD([[makeQuery(id+"F0.imprint","IMPRINT",EDGE,{"disambiguationData":[TD([[subQ2,1.0]])],"derivedFrom":subQ1}),-1.0]])]});}
            var Q65;
            {var subQ0=sQuery(id+"F0.wireOp",EDGE,"E4.10.0");var subQ1=sQuery(id+"F0.wireOp",EDGE,"E0");var subQ2=makeQuery(id+"F0.imprint","INTERSECT",VERTEX,{"derivedFrom":[subQ1,subQ0]});Q65=makeQuery(id+"F0.imprint","IMPRINT",FACE,{"disambiguationData":[TD([[makeQuery(id+"F0.imprint","IMPRINT",EDGE,{"disambiguationData":[TD([[subQ2,1.0]])],"derivedFrom":subQ1}),-1.0]])]});}
            var Q66;
            {var subQ0=sQuery(id+"F0.wireOp",EDGE,"E4.5.0");var subQ1=sQuery(id+"F0.wireOp",EDGE,"E0");var subQ2=makeQuery(id+"F0.imprint","INTERSECT",VERTEX,{"derivedFrom":[subQ1,subQ0]});Q66=makeQuery(id+"F0.imprint","IMPRINT",FACE,{"disambiguationData":[TD([[makeQuery(id+"F0.imprint","IMPRINT",EDGE,{"disambiguationData":[TD([[subQ2,1.0]])],"derivedFrom":subQ1}),-1.0]])]});}
            var Q67;
            {var subQ0=sQuery(id+"F0.wireOp",EDGE,"E4.36.0");var subQ1=sQuery(id+"F0.wireOp",EDGE,"E0");var subQ2=makeQuery(id+"F0.imprint","INTERSECT",VERTEX,{"derivedFrom":[subQ1,subQ0]});Q67=makeQuery(id+"F0.imprint","IMPRINT",FACE,{"disambiguationData":[TD([[makeQuery(id+"F0.imprint","IMPRINT",EDGE,{"disambiguationData":[TD([[subQ2,1.0]])],"derivedFrom":subQ1}),-1.0]])]});}
            var Q68;
            {var subQ0=sQuery(id+"F0.wireOp",EDGE,"E4.33.0");var subQ1=sQuery(id+"F0.wireOp",EDGE,"E0");var subQ2=makeQuery(id+"F0.imprint","INTERSECT",VERTEX,{"derivedFrom":[subQ1,subQ0]});Q68=makeQuery(id+"F0.imprint","IMPRINT",FACE,{"disambiguationData":[TD([[makeQuery(id+"F0.imprint","IMPRINT",EDGE,{"disambiguationData":[TD([[subQ2,1.0]])],"derivedFrom":subQ1}),-1.0]])]});}
            var Q69;
            {var subQ0=sQuery(id+"F0.wireOp",EDGE,"E4.42.0");var subQ1=sQuery(id+"F0.wireOp",EDGE,"E0");var subQ2=makeQuery(id+"F0.imprint","INTERSECT",VERTEX,{"derivedFrom":[subQ1,subQ0]});Q69=makeQuery(id+"F0.imprint","IMPRINT",FACE,{"disambiguationData":[TD([[makeQuery(id+"F0.imprint","IMPRINT",EDGE,{"disambiguationData":[TD([[subQ2,1.0]])],"derivedFrom":subQ1}),-1.0]])]});}
            var Q70;
            {var subQ0=sQuery(id+"F0.wireOp",EDGE,"E4.1.0");var subQ1=sQuery(id+"F0.wireOp",EDGE,"E0");var subQ2=makeQuery(id+"F0.imprint","INTERSECT",VERTEX,{"derivedFrom":[subQ1,subQ0]});Q70=makeQuery(id+"F0.imprint","IMPRINT",FACE,{"disambiguationData":[TD([[makeQuery(id+"F0.imprint","IMPRINT",EDGE,{"disambiguationData":[TD([[subQ2,1.0]])],"derivedFrom":subQ1}),-1.0]])]});}
            var Q71;
            {var subQ0=sQuery(id+"F0.wireOp",EDGE,"E4.9.0");var subQ1=sQuery(id+"F0.wireOp",EDGE,"E0");var subQ2=makeQuery(id+"F0.imprint","INTERSECT",VERTEX,{"derivedFrom":[subQ1,subQ0]});Q71=makeQuery(id+"F0.imprint","IMPRINT",FACE,{"disambiguationData":[TD([[makeQuery(id+"F0.imprint","IMPRINT",EDGE,{"disambiguationData":[TD([[subQ2,1.0]])],"derivedFrom":subQ1}),-1.0]])]});}
            var Q72;
            {var subQ0=sQuery(id+"F0.wireOp",EDGE,"E4.2.0");var subQ1=sQuery(id+"F0.wireOp",EDGE,"E0");var subQ2=makeQuery(id+"F0.imprint","INTERSECT",VERTEX,{"derivedFrom":[subQ1,subQ0]});Q72=makeQuery(id+"F0.imprint","IMPRINT",FACE,{"disambiguationData":[TD([[makeQuery(id+"F0.imprint","IMPRINT",EDGE,{"disambiguationData":[TD([[subQ2,1.0]])],"derivedFrom":subQ1}),-1.0]])]});}
            var Q73;
            {var subQ0=sQuery(id+"F0.wireOp",EDGE,"E4.7.0");var subQ1=sQuery(id+"F0.wireOp",EDGE,"E0");var subQ2=makeQuery(id+"F0.imprint","INTERSECT",VERTEX,{"derivedFrom":[subQ1,subQ0]});Q73=makeQuery(id+"F0.imprint","IMPRINT",FACE,{"disambiguationData":[TD([[makeQuery(id+"F0.imprint","IMPRINT",EDGE,{"disambiguationData":[TD([[subQ2,1.0]])],"derivedFrom":subQ1}),-1.0]])]});}
            var Q74;
            {var subQ0=sQuery(id+"F0.wireOp",EDGE,"E4.3.0");var subQ1=sQuery(id+"F0.wireOp",EDGE,"E0");var subQ2=makeQuery(id+"F0.imprint","INTERSECT",VERTEX,{"derivedFrom":[subQ1,subQ0]});Q74=makeQuery(id+"F0.imprint","IMPRINT",FACE,{"disambiguationData":[TD([[makeQuery(id+"F0.imprint","IMPRINT",EDGE,{"disambiguationData":[TD([[subQ2,1.0]])],"derivedFrom":subQ1}),-1.0]])]});}
            var Q75;
            {var subQ0=sQuery(id+"F0.wireOp",EDGE,"E4.14.0");var subQ1=sQuery(id+"F0.wireOp",EDGE,"E0");var subQ2=makeQuery(id+"F0.imprint","INTERSECT",VERTEX,{"derivedFrom":[subQ1,subQ0]});Q75=makeQuery(id+"F0.imprint","IMPRINT",FACE,{"disambiguationData":[TD([[makeQuery(id+"F0.imprint","IMPRINT",EDGE,{"disambiguationData":[TD([[subQ2,1.0]])],"derivedFrom":subQ1}),-1.0]])]});}
            var Q76;
            {var subQ0=sQuery(id+"F0.wireOp",EDGE,"E4.35.0");var subQ1=sQuery(id+"F0.wireOp",EDGE,"E0");var subQ2=makeQuery(id+"F0.imprint","INTERSECT",VERTEX,{"derivedFrom":[subQ1,subQ0]});Q76=makeQuery(id+"F0.imprint","IMPRINT",FACE,{"disambiguationData":[TD([[makeQuery(id+"F0.imprint","IMPRINT",EDGE,{"disambiguationData":[TD([[subQ2,1.0]])],"derivedFrom":subQ1}),-1.0]])]});}
            var Q77;
            {var subQ0=sQuery(id+"F0.wireOp",EDGE,"E4.6.0");var subQ1=sQuery(id+"F0.wireOp",EDGE,"E0");var subQ2=makeQuery(id+"F0.imprint","INTERSECT",VERTEX,{"derivedFrom":[subQ1,subQ0]});Q77=makeQuery(id+"F0.imprint","IMPRINT",FACE,{"disambiguationData":[TD([[makeQuery(id+"F0.imprint","IMPRINT",EDGE,{"disambiguationData":[TD([[subQ2,1.0]])],"derivedFrom":subQ1}),-1.0]])]});}
            var Q78;
            {var subQ0=sQuery(id+"F0.wireOp",EDGE,"E4.41.0");var subQ1=sQuery(id+"F0.wireOp",EDGE,"E0");var subQ2=makeQuery(id+"F0.imprint","INTERSECT",VERTEX,{"derivedFrom":[subQ1,subQ0]});Q78=makeQuery(id+"F0.imprint","IMPRINT",FACE,{"disambiguationData":[TD([[makeQuery(id+"F0.imprint","IMPRINT",EDGE,{"disambiguationData":[TD([[subQ2,1.0]])],"derivedFrom":subQ1}),-1.0]])]});}
            var Q79;
            {var subQ0=sQuery(id+"F0.wireOp",EDGE,"E4.32.0");var subQ1=sQuery(id+"F0.wireOp",EDGE,"E0");var subQ2=makeQuery(id+"F0.imprint","INTERSECT",VERTEX,{"derivedFrom":[subQ1,subQ0]});Q79=makeQuery(id+"F0.imprint","IMPRINT",FACE,{"disambiguationData":[TD([[makeQuery(id+"F0.imprint","IMPRINT",EDGE,{"disambiguationData":[TD([[subQ2,1.0]])],"derivedFrom":subQ1}),-1.0]])]});}
            var Q80;
            {var subQ0=sQuery(id+"F0.wireOp",EDGE,"E4.37.0");var subQ1=sQuery(id+"F0.wireOp",EDGE,"E0");var subQ2=makeQuery(id+"F0.imprint","INTERSECT",VERTEX,{"derivedFrom":[subQ1,subQ0]});Q80=makeQuery(id+"F0.imprint","IMPRINT",FACE,{"disambiguationData":[TD([[makeQuery(id+"F0.imprint","IMPRINT",EDGE,{"disambiguationData":[TD([[subQ2,1.0]])],"derivedFrom":subQ1}),-1.0]])]});}
            var Q81;
            {var subQ0=sQuery(id+"F0.wireOp",EDGE,"E4.40.0");var subQ1=sQuery(id+"F0.wireOp",EDGE,"E0");var subQ2=makeQuery(id+"F0.imprint","INTERSECT",VERTEX,{"derivedFrom":[subQ1,subQ0]});Q81=makeQuery(id+"F0.imprint","IMPRINT",FACE,{"disambiguationData":[TD([[makeQuery(id+"F0.imprint","IMPRINT",EDGE,{"disambiguationData":[TD([[subQ2,1.0]])],"derivedFrom":subQ1}),-1.0]])]});}
            var Q82;
            {var subQ0=sQuery(id+"F0.wireOp",EDGE,"E3");var subQ1=sQuery(id+"F0.wireOp",EDGE,"E0");var subQ2=makeQuery(id+"F0.imprint","INTERSECT",VERTEX,{"derivedFrom":[subQ1,subQ0]});Q82=makeQuery(id+"F0.imprint","IMPRINT",FACE,{"disambiguationData":[TD([[makeQuery(id+"F0.imprint","IMPRINT",EDGE,{"disambiguationData":[TD([[subQ2,-1.0]])],"derivedFrom":subQ1}),-1.0]])]});}
            var Q83;
            {var subQ0=sQuery(id+"F0.wireOp",EDGE,"E4.39.0");var subQ1=sQuery(id+"F0.wireOp",EDGE,"E0");var subQ2=makeQuery(id+"F0.imprint","INTERSECT",VERTEX,{"derivedFrom":[subQ1,subQ0]});Q83=makeQuery(id+"F0.imprint","IMPRINT",FACE,{"disambiguationData":[TD([[makeQuery(id+"F0.imprint","IMPRINT",EDGE,{"disambiguationData":[TD([[subQ2,1.0]])],"derivedFrom":subQ1}),-1.0]])]});}
            var Q84;
            {var subQ0=sQuery(id+"F0.wireOp",EDGE,"E4.8.0");var subQ1=sQuery(id+"F0.wireOp",EDGE,"E0");var subQ2=makeQuery(id+"F0.imprint","INTERSECT",VERTEX,{"derivedFrom":[subQ1,subQ0]});Q84=makeQuery(id+"F0.imprint","IMPRINT",FACE,{"disambiguationData":[TD([[makeQuery(id+"F0.imprint","IMPRINT",EDGE,{"disambiguationData":[TD([[subQ2,1.0]])],"derivedFrom":subQ1}),-1.0]])]});}
            var Q85;
            {var subQ0=sQuery(id+"F0.wireOp",EDGE,"E4.34.0");var subQ1=sQuery(id+"F0.wireOp",EDGE,"E0");var subQ2=makeQuery(id+"F0.imprint","INTERSECT",VERTEX,{"derivedFrom":[subQ1,subQ0]});Q85=makeQuery(id+"F0.imprint","IMPRINT",FACE,{"disambiguationData":[TD([[makeQuery(id+"F0.imprint","IMPRINT",EDGE,{"disambiguationData":[TD([[subQ2,1.0]])],"derivedFrom":subQ1}),-1.0]])]});}
            var Q86;
            {var subQ0=sQuery(id+"F0.wireOp",EDGE,"E2");var subQ1=sQuery(id+"F0.wireOp",EDGE,"E0");var subQ2=makeQuery(id+"F0.imprint","INTERSECT",VERTEX,{"derivedFrom":[subQ1,subQ0]});Q86=makeQuery(id+"F0.imprint","IMPRINT",FACE,{"disambiguationData":[TD([[makeQuery(id+"F0.imprint","IMPRINT",EDGE,{"disambiguationData":[TD([[subQ2,1.0]])],"derivedFrom":subQ1}),-1.0]])]});}
            var Q87;
            {var subQ0=sQuery(id+"F0.wireOp",EDGE,"E4.4.0");var subQ1=sQuery(id+"F0.wireOp",EDGE,"E0");var subQ2=makeQuery(id+"F0.imprint","INTERSECT",VERTEX,{"derivedFrom":[subQ1,subQ0]});Q87=makeQuery(id+"F0.imprint","IMPRINT",FACE,{"disambiguationData":[TD([[makeQuery(id+"F0.imprint","IMPRINT",EDGE,{"disambiguationData":[TD([[subQ2,1.0]])],"derivedFrom":subQ1}),-1.0]])]});}
            var Q88;
            {var subQ0=sQuery(id+"F0.wireOp",EDGE,"E4.15.0");var subQ1=sQuery(id+"F0.wireOp",EDGE,"E0");var subQ2=makeQuery(id+"F0.imprint","INTERSECT",VERTEX,{"derivedFrom":[subQ1,subQ0]});Q88=makeQuery(id+"F0.imprint","IMPRINT",FACE,{"disambiguationData":[TD([[makeQuery(id+"F0.imprint","IMPRINT",EDGE,{"disambiguationData":[TD([[subQ2,1.0]])],"derivedFrom":subQ1}),-1.0]])]});}
            var Q89;
            {var subQ0=sQuery(id+"F0.wireOp",EDGE,"E4.31.0");var subQ1=sQuery(id+"F0.wireOp",EDGE,"E0");var subQ2=makeQuery(id+"F0.imprint","INTERSECT",VERTEX,{"derivedFrom":[subQ1,subQ0]});Q89=makeQuery(id+"F0.imprint","IMPRINT",FACE,{"disambiguationData":[TD([[makeQuery(id+"F0.imprint","IMPRINT",EDGE,{"disambiguationData":[TD([[subQ2,1.0]])],"derivedFrom":subQ1}),-1.0]])]});}
            extrude(context, id + "F1", {"entities" : qUnion([Q0, Q1, Q2, Q3, Q4, Q5, Q6, Q7, Q8, Q9, Q10, Q11, Q12, Q13, Q14, Q15, Q16, Q17, Q18, Q19, Q20, Q21, Q22, Q23, Q24, Q25, Q26, Q27, Q28, Q29, Q30, Q31, Q32, Q33, Q34, Q35, Q36, Q37, Q38, Q39, Q40, Q41, Q42, Q43, Q44, Q45, Q46, Q47, Q48, Q49, Q50, Q51, Q52, Q53, Q54, Q55, Q56, Q57, Q58, Q59, Q60, Q61, Q62, Q63, Q64, Q65, Q66, Q67, Q68, Q69, Q70, Q71, Q72, Q73, Q74, Q75, Q76, Q77, Q78, Q79, Q80, Q81, Q82, Q83, Q84, Q85, Q86, Q87, Q88, Q89]), "depth" : 12.7 * mm});
        }
        {
            var Q0;
            Q0=makeQuery(id+"F0.imprint","IMPRINT",FACE,{"disambiguationData":[TD([[makeQuery(id+"F0.imprint","IMPRINT",EDGE,{"derivedFrom":sQuery(id+"F0.wireOp",EDGE,"E1")}),1.0]])]});
            extrude(context, id + "F2", {"entities" : qUnion([Q0]), "operationType" : NewBodyOperationType.ADD, "depth" : 12.7 * mm});
        }
        {
            var Q0;
            Q0=makeQuery(id+"F0.imprint","IMPRINT",FACE,{"disambiguationData":[TD([[makeQuery(id+"F0.imprint","IMPRINT",EDGE,{"derivedFrom":sQuery(id+"F0.wireOp",EDGE,"E1")}),1.0]])]});
            extrude(context, id + "F3", {"entities" : qUnion([Q0]), "operationType" : NewBodyOperationType.ADD, "depth" : 12.7 * mm});
        }
    });
